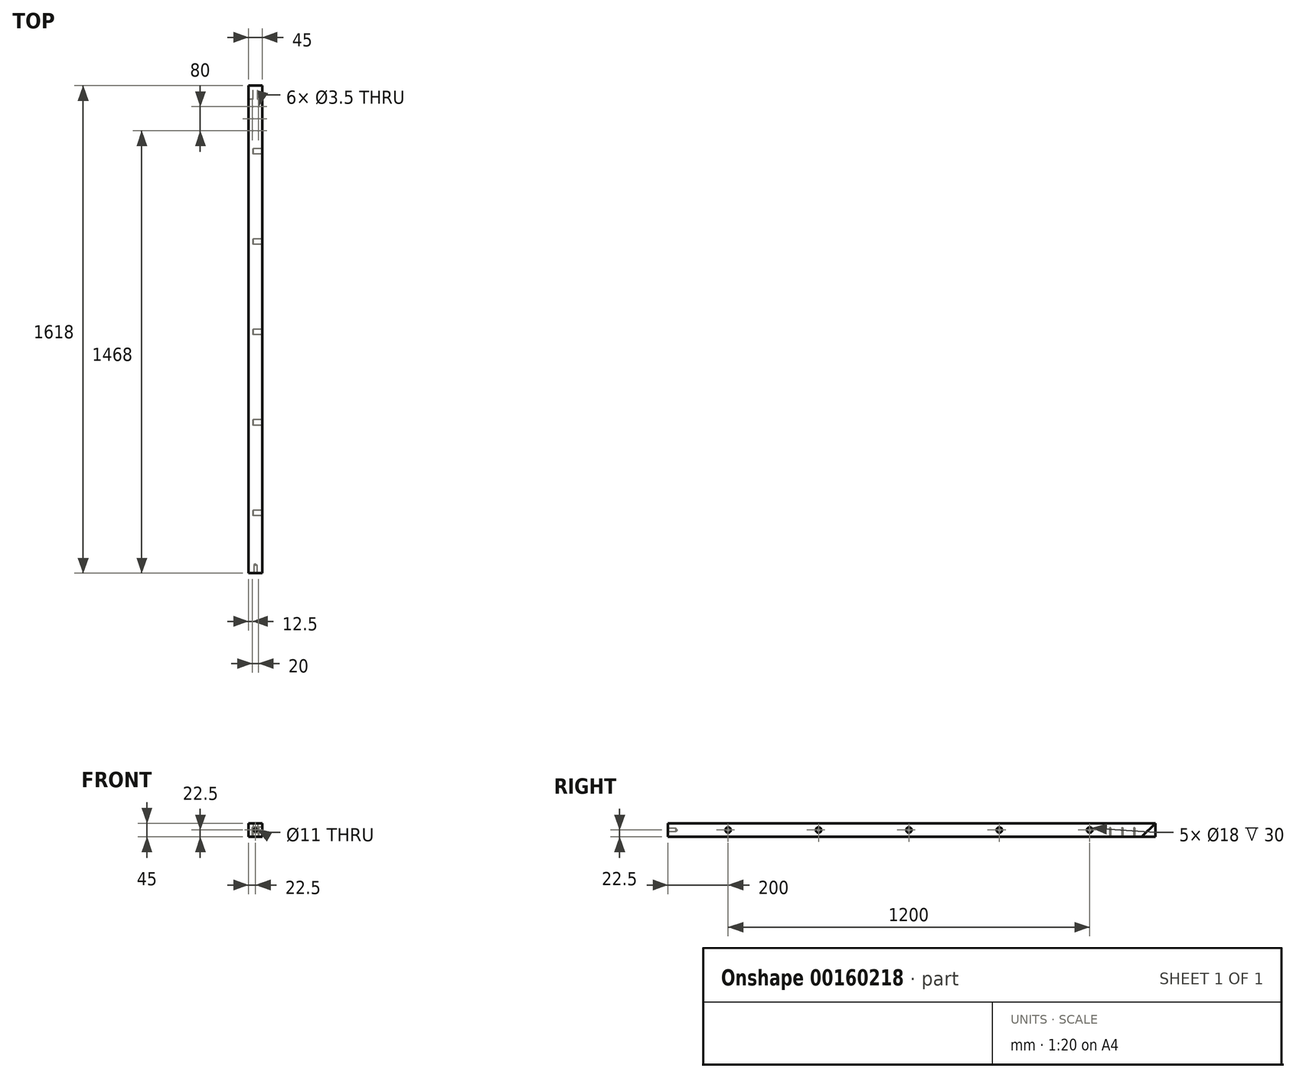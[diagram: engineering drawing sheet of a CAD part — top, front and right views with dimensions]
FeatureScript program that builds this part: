
annotation { "Feature Type Name" : "Feature", "Feature Type Description" : "" }
export const myFeature = defineFeature(function(context is Context, id is Id, definition is map)
    precondition{}
    {
        {
            var Q0;
            Q0=qCreatedBy(makeId("Right.planeOp"),FACE);
            var sketch = newSketch(context, id + "F0", { "sketchPlane" : qUnion([Q0])});
            skLineSegment(sketch, "E0.bottom", {"start": v(0, 22.5) * mm, "end": v(1618, 22.5) * mm});
            skLineSegment(sketch, "E0.top", {"start": v(0, -22.5) * mm, "end": v(1618, -22.5) * mm});
            skLineSegment(sketch, "E0.left", {"start": v(0, 22.5) * mm, "end": v(0, -22.5) * mm});
            skLineSegment(sketch, "E0.right", {"start": v(1618, 22.5) * mm, "end": v(1618, -22.5) * mm});
            skSolve(sketch);
        }
        {
            var Q0;
            Q0=makeQuery(id+"F0.imprint","IMPRINT",FACE,{"disambiguationData":[TD([[makeQuery(id+"F0.imprint","IMPRINT",EDGE,{"derivedFrom":sQuery(id+"F0.wireOp",EDGE,"E0.bottom")}),-1.0]])]});
            extrude(context, id + "F1", {"entities" : qUnion([Q0]), "endBound" : BoundingType.SYMMETRIC, "depth" : 45 * mm});
        }
        {
            var Q0;
            Q0=makeQuery(id+"F1.opExtrude","SWEPT_FACE",FACE,{"disambiguationData":[OSD([sQuery(id+"F0.wireOp",EDGE,"E0.left")])]});
            var sketch = newSketch(context, id + "F2", { "sketchPlane" : qUnion([Q0])});
            skPoint(sketch, "E1", {"position": v(0, 0) * mm});
            skSolve(sketch);
        }
        {
            var Q0;
            Q0=sQuery(id+"F2.wireOp",VERTEX,"E1");
            var Q1;
            Q1=makeQuery(id+"F1.opExtrude","SWEPT_BODY",BODY,{"disambiguationData":[OSD([sQuery(id+"F0.wireOp",EDGE,"E0.bottom"),sQuery(id+"F0.wireOp",EDGE,"E0.top"),sQuery(id+"F0.wireOp",EDGE,"E0.left"),sQuery(id+"F0.wireOp",EDGE,"E0.right")])]});
            hole(context, id + "F3", {"style" : HoleStyle.SIMPLE, "endStyle" : HoleEndStyle.BLIND, "holeDiameter" : 11 * mm, "holeDepth" : 27 * mm, "startFromSketch" : true, "locations" : qUnion([Q0]), "scope" : qUnion([Q1])});
        }
        {
            var Q0;
            Q0=makeQuery(id+"F1.opExtrude","CAP_FACE",FACE,{"disambiguationData":[OSD([sQuery(id+"F0.wireOp",EDGE,"E0.bottom"),sQuery(id+"F0.wireOp",EDGE,"E0.top"),sQuery(id+"F0.wireOp",EDGE,"E0.left"),sQuery(id+"F0.wireOp",EDGE,"E0.right")])],"isStart":false});
            var sketch = newSketch(context, id + "F4", { "sketchPlane" : qUnion([Q0])});
            skLineSegment(sketch, "E2", {"start": v(1618, 22.5) * mm, "end": v(1573, -22.5) * mm});
            skSolve(sketch);
        }
        {
            var Q0;
            {var subQ0=sQuery(id+"F4.wireOp",EDGE,"E2");Q0=makeQuery(id+"F4.imprint","IMPRINT",FACE,{"disambiguationData":[TD([[makeQuery(id+"F4.imprint","IMPRINT",EDGE,{"derivedFrom":subQ0}),1.0]])]});}
            extrude(context, id + "F5", {"entities" : qUnion([Q0]), "operationType" : NewBodyOperationType.REMOVE, "oppositeDirection" : true, "depth" : 15 * mm});
        }
        {
            var Q0;
            Q0=makeQuery(id+"F1.opExtrude","CAP_FACE",FACE,{"disambiguationData":[OSD([sQuery(id+"F0.wireOp",EDGE,"E0.bottom"),sQuery(id+"F0.wireOp",EDGE,"E0.top"),sQuery(id+"F0.wireOp",EDGE,"E0.left"),sQuery(id+"F0.wireOp",EDGE,"E0.right")])],"isStart":true});
            var sketch = newSketch(context, id + "F6", { "sketchPlane" : qUnion([Q0])});
            skLineSegment(sketch, "E3", {"start": v(-1618, 22.5) * mm, "end": v(-1573, -22.5) * mm});
            skSolve(sketch);
        }
        {
            var Q0;
            {var subQ0=sQuery(id+"F6.wireOp",EDGE,"E3");Q0=makeQuery(id+"F6.imprint","IMPRINT",FACE,{"disambiguationData":[TD([[makeQuery(id+"F6.imprint","IMPRINT",EDGE,{"derivedFrom":subQ0}),-1.0]])]});}
            extrude(context, id + "F7", {"entities" : qUnion([Q0]), "operationType" : NewBodyOperationType.REMOVE, "oppositeDirection" : true, "depth" : 15 * mm});
        }
        {
            var Q0;
            Q0=makeQuery(id+"F1.opExtrude","CAP_FACE",FACE,{"disambiguationData":[OSD([sQuery(id+"F0.wireOp",EDGE,"E0.bottom"),sQuery(id+"F0.wireOp",EDGE,"E0.top"),sQuery(id+"F0.wireOp",EDGE,"E0.left"),sQuery(id+"F0.wireOp",EDGE,"E0.right")])],"isStart":true});
            var sketch = newSketch(context, id + "F8", { "sketchPlane" : qUnion([Q0])});
            skCircle(sketch, "E4", {"center": v(-200, 0) * mm, "radius": 9 * mm});
            skCircle(sketch, "E5", {"center": v(-500, 0) * mm, "radius": 9 * mm});
            skCircle(sketch, "E6", {"center": v(-800, 0) * mm, "radius": 9 * mm});
            skCircle(sketch, "E7", {"center": v(-1100, 0) * mm, "radius": 9 * mm});
            skCircle(sketch, "E8", {"center": v(-1400, 0) * mm, "radius": 9 * mm});
            skSolve(sketch);
        }
        {
            var Q0;
            Q0=makeQuery(id+"F8.imprint","IMPRINT",FACE,{"disambiguationData":[TD([[makeQuery(id+"F8.imprint","IMPRINT",EDGE,{"derivedFrom":sQuery(id+"F8.wireOp",EDGE,"E4")}),1.0]])]});
            var Q1;
            Q1=makeQuery(id+"F8.imprint","IMPRINT",FACE,{"disambiguationData":[TD([[makeQuery(id+"F8.imprint","IMPRINT",EDGE,{"derivedFrom":sQuery(id+"F8.wireOp",EDGE,"E5")}),1.0]])]});
            var Q2;
            Q2=makeQuery(id+"F8.imprint","IMPRINT",FACE,{"disambiguationData":[TD([[makeQuery(id+"F8.imprint","IMPRINT",EDGE,{"derivedFrom":sQuery(id+"F8.wireOp",EDGE,"E6")}),1.0]])]});
            var Q3;
            Q3=makeQuery(id+"F8.imprint","IMPRINT",FACE,{"disambiguationData":[TD([[makeQuery(id+"F8.imprint","IMPRINT",EDGE,{"derivedFrom":sQuery(id+"F8.wireOp",EDGE,"E7")}),1.0]])]});
            var Q4;
            Q4=makeQuery(id+"F8.imprint","IMPRINT",FACE,{"disambiguationData":[TD([[makeQuery(id+"F8.imprint","IMPRINT",EDGE,{"derivedFrom":sQuery(id+"F8.wireOp",EDGE,"E8")}),1.0]])]});
            extrude(context, id + "F9", {"entities" : qUnion([Q0, Q1, Q2, Q3, Q4]), "operationType" : NewBodyOperationType.REMOVE, "endBound" : BoundingType.THROUGH_ALL, "oppositeDirection" : true, "depth" : 25 * mm});
        }
        {
            var Q0;
            Q0=makeQuery(id+"F8.imprint","IMPRINT",FACE,{"disambiguationData":[TD([[makeQuery(id+"F8.imprint","IMPRINT",EDGE,{"derivedFrom":sQuery(id+"F8.wireOp",EDGE,"E8")}),1.0]])]});
            var Q1;
            Q1=makeQuery(id+"F8.imprint","IMPRINT",FACE,{"disambiguationData":[TD([[makeQuery(id+"F8.imprint","IMPRINT",EDGE,{"derivedFrom":sQuery(id+"F8.wireOp",EDGE,"E7")}),1.0]])]});
            var Q2;
            Q2=makeQuery(id+"F8.imprint","IMPRINT",FACE,{"disambiguationData":[TD([[makeQuery(id+"F8.imprint","IMPRINT",EDGE,{"derivedFrom":sQuery(id+"F8.wireOp",EDGE,"E6")}),1.0]])]});
            var Q3;
            Q3=makeQuery(id+"F8.imprint","IMPRINT",FACE,{"disambiguationData":[TD([[makeQuery(id+"F8.imprint","IMPRINT",EDGE,{"derivedFrom":sQuery(id+"F8.wireOp",EDGE,"E5")}),1.0]])]});
            var Q4;
            Q4=makeQuery(id+"F8.imprint","IMPRINT",FACE,{"disambiguationData":[TD([[makeQuery(id+"F8.imprint","IMPRINT",EDGE,{"derivedFrom":sQuery(id+"F8.wireOp",EDGE,"E4")}),1.0]])]});
            extrude(context, id + "F10", {"entities" : qUnion([Q0, Q1, Q2, Q3, Q4]), "operationType" : NewBodyOperationType.ADD, "oppositeDirection" : true, "depth" : 15 * mm});
        }
        {
            var Q0;
            Q0=makeQuery(id+"F1.opExtrude","SWEPT_FACE",FACE,{"disambiguationData":[OSD([sQuery(id+"F0.wireOp",EDGE,"E0.top")])]});
            var sketch = newSketch(context, id + "F11", { "sketchPlane" : qUnion([Q0])});
            skPoint(sketch, "E9", {"position": v(-22.5, -1573) * mm});
            skPoint(sketch, "E10", {"position": v(-22.5, 0) * mm});
            skPoint(sketch, "E11", {"position": v(10, -1548) * mm});
            skPoint(sketch, "E12", {"position": v(10, -1508) * mm});
            skPoint(sketch, "E13", {"position": v(10, -1468) * mm});
            skPoint(sketch, "E14", {"position": v(-10, -1548) * mm});
            skPoint(sketch, "E15", {"position": v(-10, -1508) * mm});
            skPoint(sketch, "E16", {"position": v(-10, -1468) * mm});
            skSolve(sketch);
        }
        {
            var Q0;
            Q0=sQuery(id+"F11.wireOp",VERTEX,"E11");
            var Q1;
            Q1=sQuery(id+"F11.wireOp",VERTEX,"E12");
            var Q2;
            Q2=sQuery(id+"F11.wireOp",VERTEX,"E13");
            var Q3;
            Q3=sQuery(id+"F11.wireOp",VERTEX,"E16");
            var Q4;
            Q4=sQuery(id+"F11.wireOp",VERTEX,"E15");
            var Q5;
            Q5=sQuery(id+"F11.wireOp",VERTEX,"E14");
            var Q6;
            Q6=makeQuery(id+"F1.opExtrude","SWEPT_BODY",BODY,{"disambiguationData":[OSD([sQuery(id+"F0.wireOp",EDGE,"E0.bottom"),sQuery(id+"F0.wireOp",EDGE,"E0.top"),sQuery(id+"F0.wireOp",EDGE,"E0.left"),sQuery(id+"F0.wireOp",EDGE,"E0.right")])]});
            hole(context, id + "F12", {"style" : HoleStyle.SIMPLE, "endStyle" : HoleEndStyle.BLIND, "holeDiameter" : 3.5 * mm, "holeDepth" : 30 * mm, "startFromSketch" : true, "locations" : qUnion([Q0, Q1, Q2, Q3, Q4, Q5]), "scope" : qUnion([Q6])});
        }
    });
